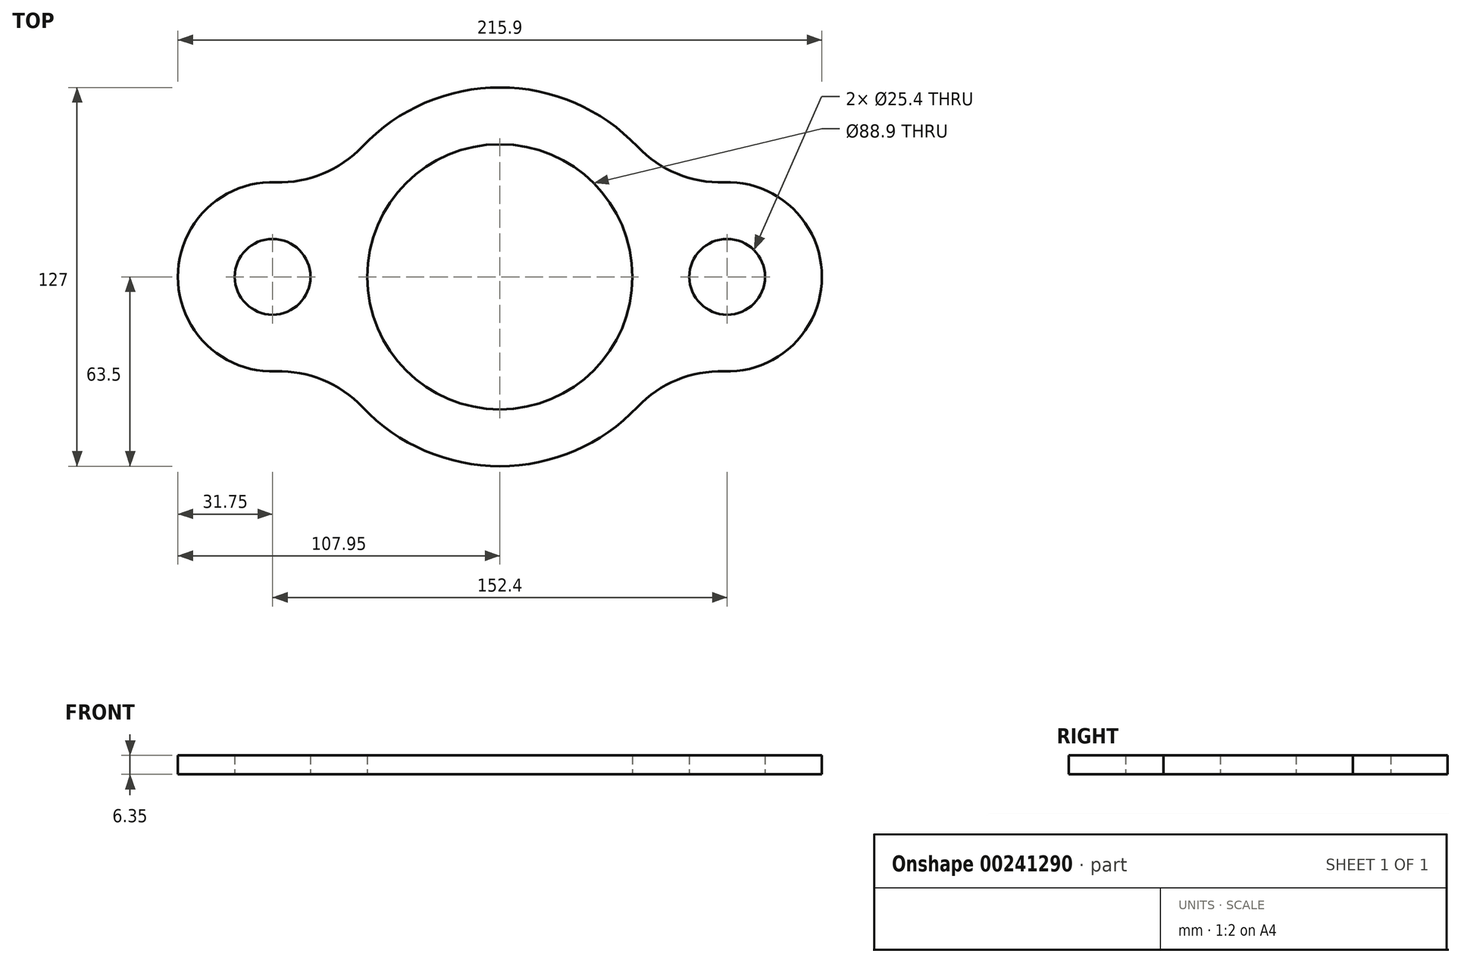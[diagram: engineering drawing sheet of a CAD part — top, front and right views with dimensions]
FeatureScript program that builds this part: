
annotation { "Feature Type Name" : "Feature", "Feature Type Description" : "" }
export const myFeature = defineFeature(function(context is Context, id is Id, definition is map)
    precondition{}
    {
        {
            var Q0;
            Q0=qCreatedBy(makeId("Top.planeOp"),FACE);
            var sketch = newSketch(context, id + "F0", { "sketchPlane" : qUnion([Q0])});
            skCircle(sketch, "E0", {"center": v(0, 0) * mm, "radius": 44.45 * mm});
            skArc(sketch, "E1", {"start": v(-46.14, -43.63) * mm, "mid": v(0, -63.5) * mm, "end": v(46.14, -43.63) * mm});
            skCircle(sketch, "E2", {"center": v(-76.2, 0) * mm, "radius": 12.7 * mm});
            skCircle(sketch, "E3", {"center": v(76.2, 0) * mm, "radius": 12.7 * mm});
            skArc(sketch, "E4", {"start": v(-75.12, 31.73) * mm, "mid": v(-107.95, 0) * mm, "end": v(-75.12, -31.73) * mm});
            skArc(sketch, "E5", {"start": v(75.12, -31.73) * mm, "mid": v(107.95, 0) * mm, "end": v(75.12, 31.73) * mm});
            skArc(sketch, "E6.trimOffspring", {"start": v(46.14, 43.63) * mm, "mid": v(0, 63.5) * mm, "end": v(-46.14, 43.63) * mm});
            skPoint(sketch, "E7.visualSharp", {"position": v(-57.94, 25.98) * mm});
            skArc(sketch, "E7.filletArc", {"start": v(-75.12, 31.73) * mm, "mid": v(-59.35, 34.56) * mm, "end": v(-46.14, 43.63) * mm});
            skPoint(sketch, "E8.visualSharp", {"position": v(57.94, 25.98) * mm});
            skArc(sketch, "E8.filletArc", {"start": v(46.14, 43.63) * mm, "mid": v(59.35, 34.56) * mm, "end": v(75.12, 31.73) * mm});
            skPoint(sketch, "E9.visualSharp", {"position": v(57.94, -25.98) * mm});
            skArc(sketch, "E9.filletArc", {"start": v(75.12, -31.73) * mm, "mid": v(59.35, -34.56) * mm, "end": v(46.14, -43.63) * mm});
            skPoint(sketch, "E10.visualSharp", {"position": v(-57.94, -25.98) * mm});
            skArc(sketch, "E10.filletArc", {"start": v(-46.14, -43.63) * mm, "mid": v(-59.35, -34.56) * mm, "end": v(-75.12, -31.73) * mm});
            skSolve(sketch);
        }
        {
            var Q0;
            Q0=makeQuery(id+"F0.imprint","IMPRINT",FACE,{"disambiguationData":[TD([[makeQuery(id+"F0.imprint","IMPRINT",EDGE,{"derivedFrom":sQuery(id+"F0.wireOp",EDGE,"E0")}),-1.0]])]});
            extrude(context, id + "F1", {"entities" : qUnion([Q0]), "depth" : 6.35 * mm});
        }
    });
